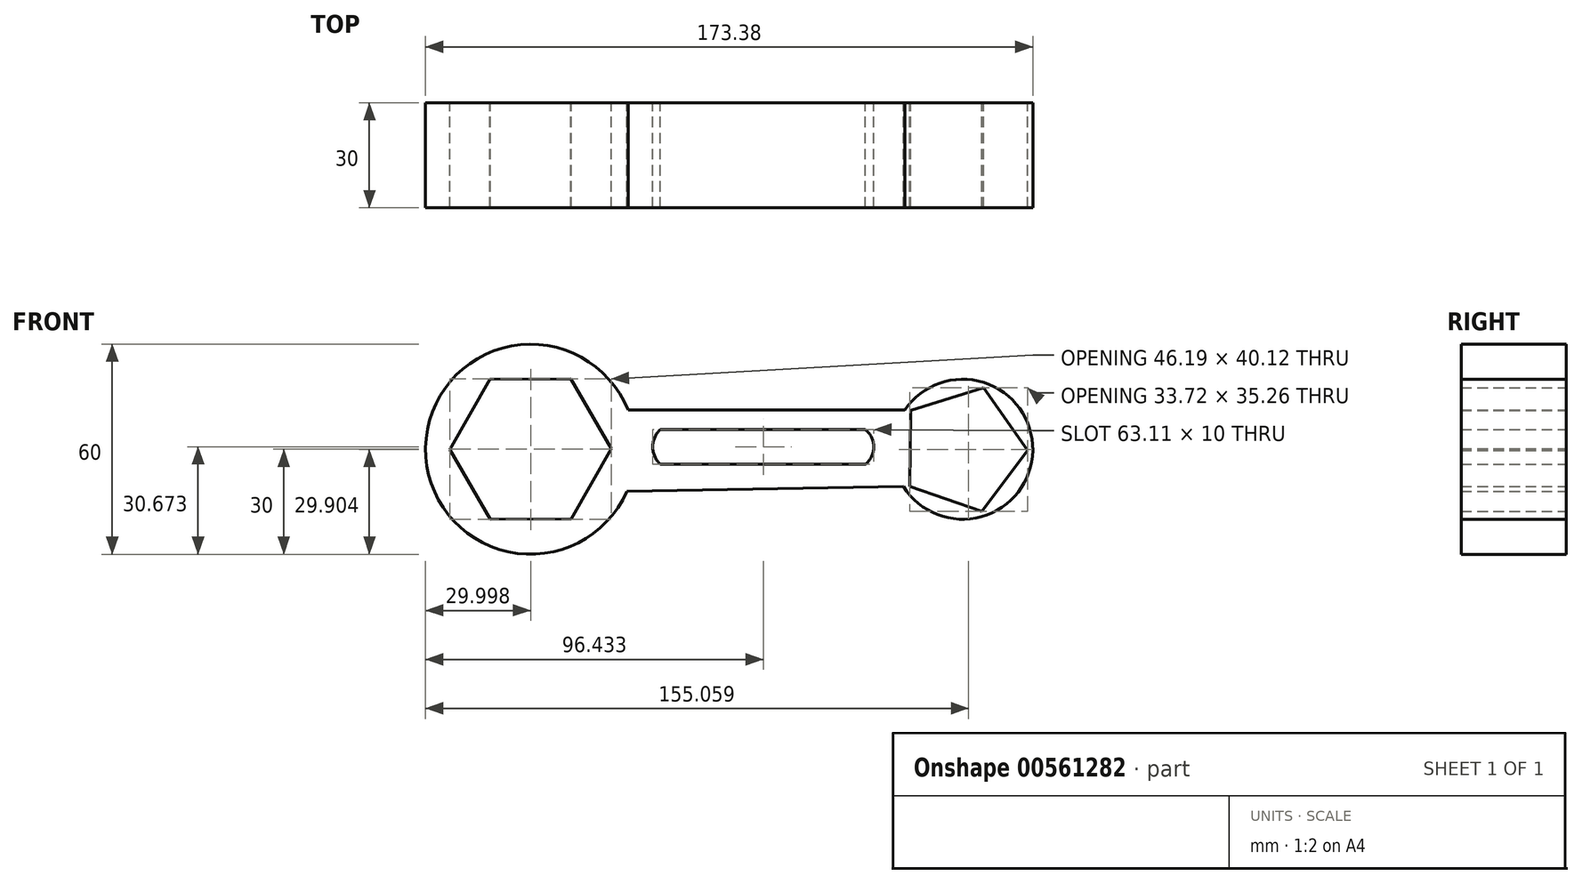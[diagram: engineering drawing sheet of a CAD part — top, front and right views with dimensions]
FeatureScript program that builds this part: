
annotation { "Feature Type Name" : "Feature", "Feature Type Description" : "" }
export const myFeature = defineFeature(function(context is Context, id is Id, definition is map)
    precondition{}
    {
        {
            var Q0;
            Q0=qCreatedBy(makeId("Front.planeOp"),FACE);
            var sketch = newSketch(context, id + "F0", { "sketchPlane" : qUnion([Q0])});
            skPoint(sketch, "E0.center.orphan", {"position": v(-42.18, 0) * mm});
            skCircle(sketch, "E1", {"center": v(-42.18, 0) * mm, "radius": 30 * mm});
            skCircle(sketch, "E2.cCircle", {"center": v(-42.18, 0) * mm, "radius": 20 * mm, "construction": true});
            skLineSegment(sketch, "E2.0", {"start": v(-19.09, 0.12) * mm, "end": v(-30.53, -19.94) * mm});
            skLineSegment(sketch, "E2.1", {"start": v(-30.53, -19.94) * mm, "end": v(-53.63, -20.06) * mm});
            skLineSegment(sketch, "E2.2", {"start": v(-53.63, -20.06) * mm, "end": v(-65.28, -0.12) * mm});
            skLineSegment(sketch, "E2.3", {"start": v(-65.28, -0.12) * mm, "end": v(-53.83, 19.94) * mm});
            skLineSegment(sketch, "E2.4", {"start": v(-53.83, 19.94) * mm, "end": v(-30.74, 20.06) * mm});
            skLineSegment(sketch, "E2.5", {"start": v(-30.74, 20.06) * mm, "end": v(-19.09, 0.12) * mm});
            skPoint(sketch, "E2.0.midPoint", {"position": v(-24.81, -9.91) * mm});
            skCircle(sketch, "E3", {"center": v(81.2, 0) * mm, "radius": 20 * mm});
            skPoint(sketch, "E4.visualSharp", {"position": v(84.3, 11.22) * mm});
            skPoint(sketch, "E5.visualSharp", {"position": v(86.47, -0.9) * mm});
            skArc(sketch, "E5.filletArc", {"start": v(66.78, -13.6) * mm, "mid": v(66.93, -12.78) * mm, "end": v(66.95, -11.96) * mm});
            skCircle(sketch, "E6.cCircle", {"center": v(81.2, 0) * mm, "radius": 15 * mm, "construction": true});
            skLineSegment(sketch, "E6.0", {"start": v(99.74, -0.31) * mm, "end": v(86.63, -17.73) * mm});
            skLineSegment(sketch, "E6.1", {"start": v(86.63, -17.73) * mm, "end": v(66.02, -10.65) * mm});
            skLineSegment(sketch, "E6.2", {"start": v(66.02, -10.65) * mm, "end": v(66.38, 11.15) * mm});
            skLineSegment(sketch, "E6.3", {"start": v(66.38, 11.15) * mm, "end": v(87.22, 17.54) * mm});
            skLineSegment(sketch, "E6.4", {"start": v(87.22, 17.54) * mm, "end": v(99.74, -0.31) * mm});
            skPoint(sketch, "E6.0.midPoint", {"position": v(93.19, -9.02) * mm});
            skPoint(sketch, "E7.orphan", {"position": v(-14.36, 11.22) * mm});
            skPoint(sketch, "E8.orphan", {"position": v(-12.2, -0.9) * mm});
            skPoint(sketch, "E9.visualSharp", {"position": v(22.37, -0.9) * mm});
            skLineSegment(sketch, "E10.trimOffspring", {"start": v(66.2, -0.03) * mm, "end": v(66.3, -1.81) * mm});
            skLineSegment(sketch, "E11", {"start": v(-14.36, 11.22) * mm, "end": v(64.64, 11.22) * mm});
            skLineSegment(sketch, "E12", {"start": v(-14.72, -12.07) * mm, "end": v(64.27, -10.65) * mm});
            skLineSegment(sketch, "E13", {"start": v(-5.15, 5.67) * mm, "end": v(53.4, 5.67) * mm});
            skLineSegment(sketch, "E14", {"start": v(53.4, -4.33) * mm, "end": v(-5.15, -4.33) * mm});
            skArc(sketch, "E15", {"start": v(-5.15, 5.67) * mm, "mid": v(-7.3, 0.67) * mm, "end": v(-5.15, -4.33) * mm});
            skArc(sketch, "E16", {"start": v(53.4, -4.33) * mm, "mid": v(55.8, 0.67) * mm, "end": v(53.4, 5.67) * mm});
            skSolve(sketch);
        }
        {
            var Q0;
            Q0 = qSketchRegion(id + "F0", true);
            extrude(context, id + "F1", {"entities" : qUnion([Q0]), "depth" : 30 * mm, "offsetDistance" : 25 * mm});
        }
    });
